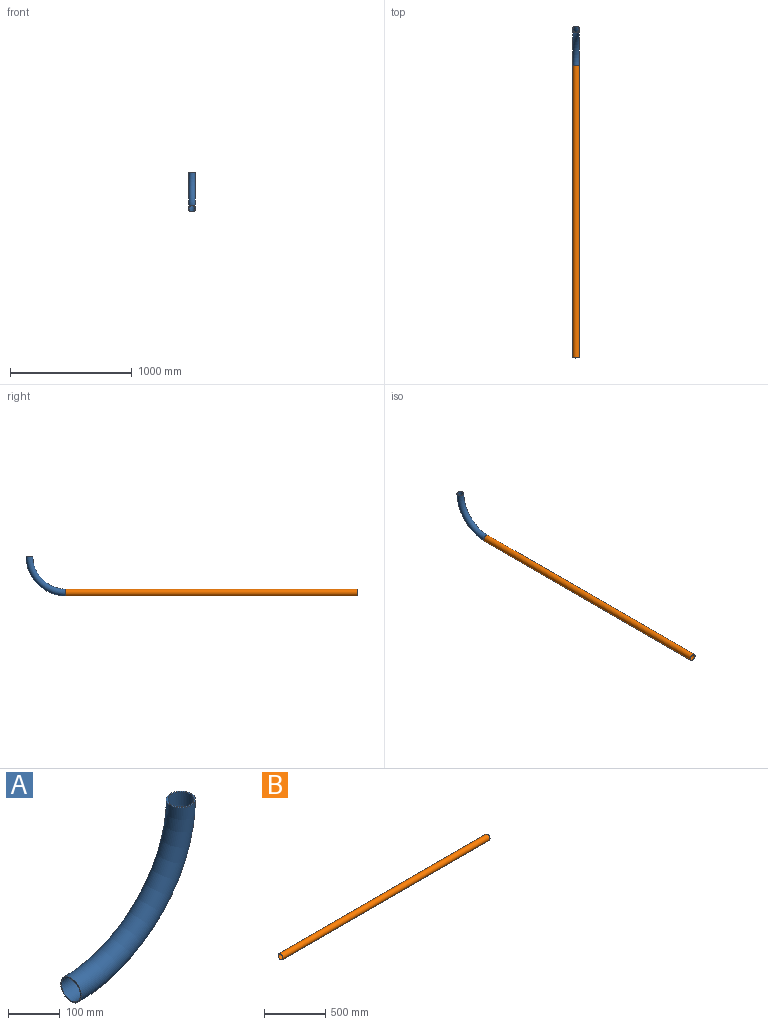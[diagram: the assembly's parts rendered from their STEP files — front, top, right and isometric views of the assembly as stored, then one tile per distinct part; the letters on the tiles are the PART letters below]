
ASSEMBLY  parts=2 mates=1
PART A: 4 faces, bbox 355x56x355 mm
  f0: torus R=300mm, axis (0,-1,0), area 75502.5mm2, adj f1,f2
  f1: plane 56x56mm, normal (-1,0,0), area 420.2mm2, adj f0,f3
  f2: plane 56x56mm, normal (0,0,1), area 420.2mm2, adj f0,f3
  f3: torus R=300mm, axis (0,-1,0), area 82904.7mm2, adj f1,f2
PART B: 4 faces, bbox 2400x56x56 mm
  f0: cylinder r=25.5mm len=2400mm, axis (-1,0,0), area 384530.9mm2, adj f2,f3
  f1: cylinder r=28mm len=2400mm, axis (-1,0,0), area 422230.1mm2, adj f2,f3
  f2: plane 56x56mm, normal (1,0,0), area 420.2mm2, adj f0,f1
  f3: plane 56x56mm, normal (-1,0,0), area 420.2mm2, adj f0,f1
PLACE A rot(axis=(0,0,1),90deg) t=(0,-300,-249)mm fixed
PLACE B rot(axis=(-0.58,-0.58,0.58),120deg) t=(0,-2700,-249)mm
MATE fastened A.f1 <-> B.f1  axis (0,-1,0) through (0,-300,-249)mm
